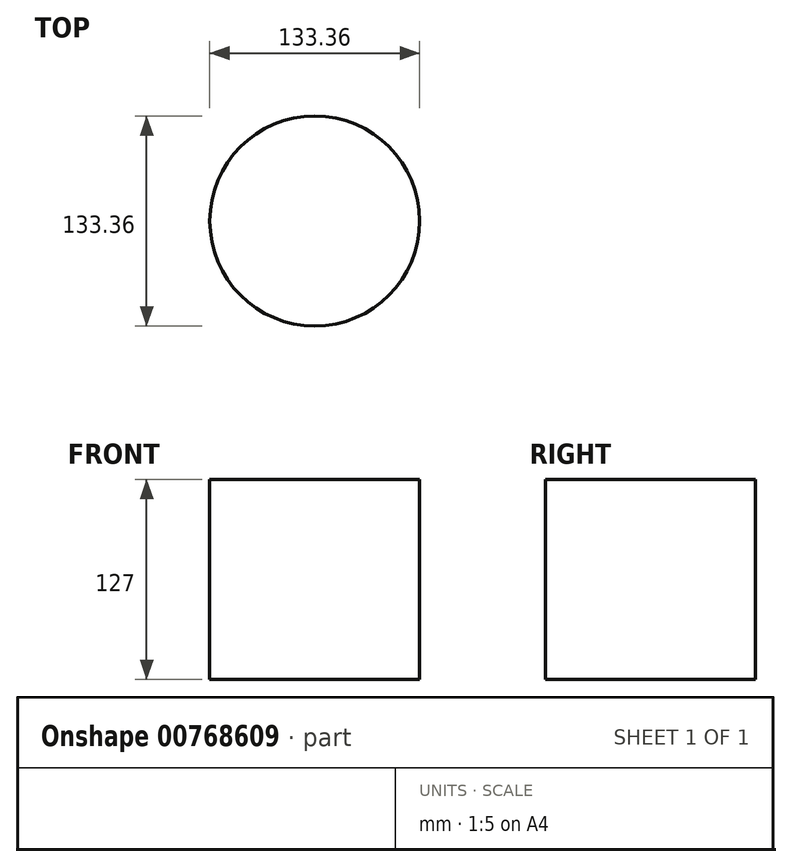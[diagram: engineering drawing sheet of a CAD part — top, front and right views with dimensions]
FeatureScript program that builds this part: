
annotation { "Feature Type Name" : "Feature", "Feature Type Description" : "" }
export const myFeature = defineFeature(function(context is Context, id is Id, definition is map)
    precondition{}
    {
        {
            var Q0;
            Q0=qCreatedBy(makeId("Top.planeOp"),FACE);
            var sketch = newSketch(context, id + "F0", { "sketchPlane" : qUnion([Q0])});
            skCircle(sketch, "E0", {"center": v(0, 0) * mm, "radius": 66.68 * mm});
            skSolve(sketch);
        }
        {
            var Q0;
            Q0=sQuery(id+"F0.wireOp",EDGE,"E0");
            extrude(context, id + "F1", {"bodyType" : ToolBodyType.SURFACE, "surfaceEntities" : qUnion([Q0]), "depth" : 127 * mm, "offsetDistance" : 25.4 * mm});
        }
    });
